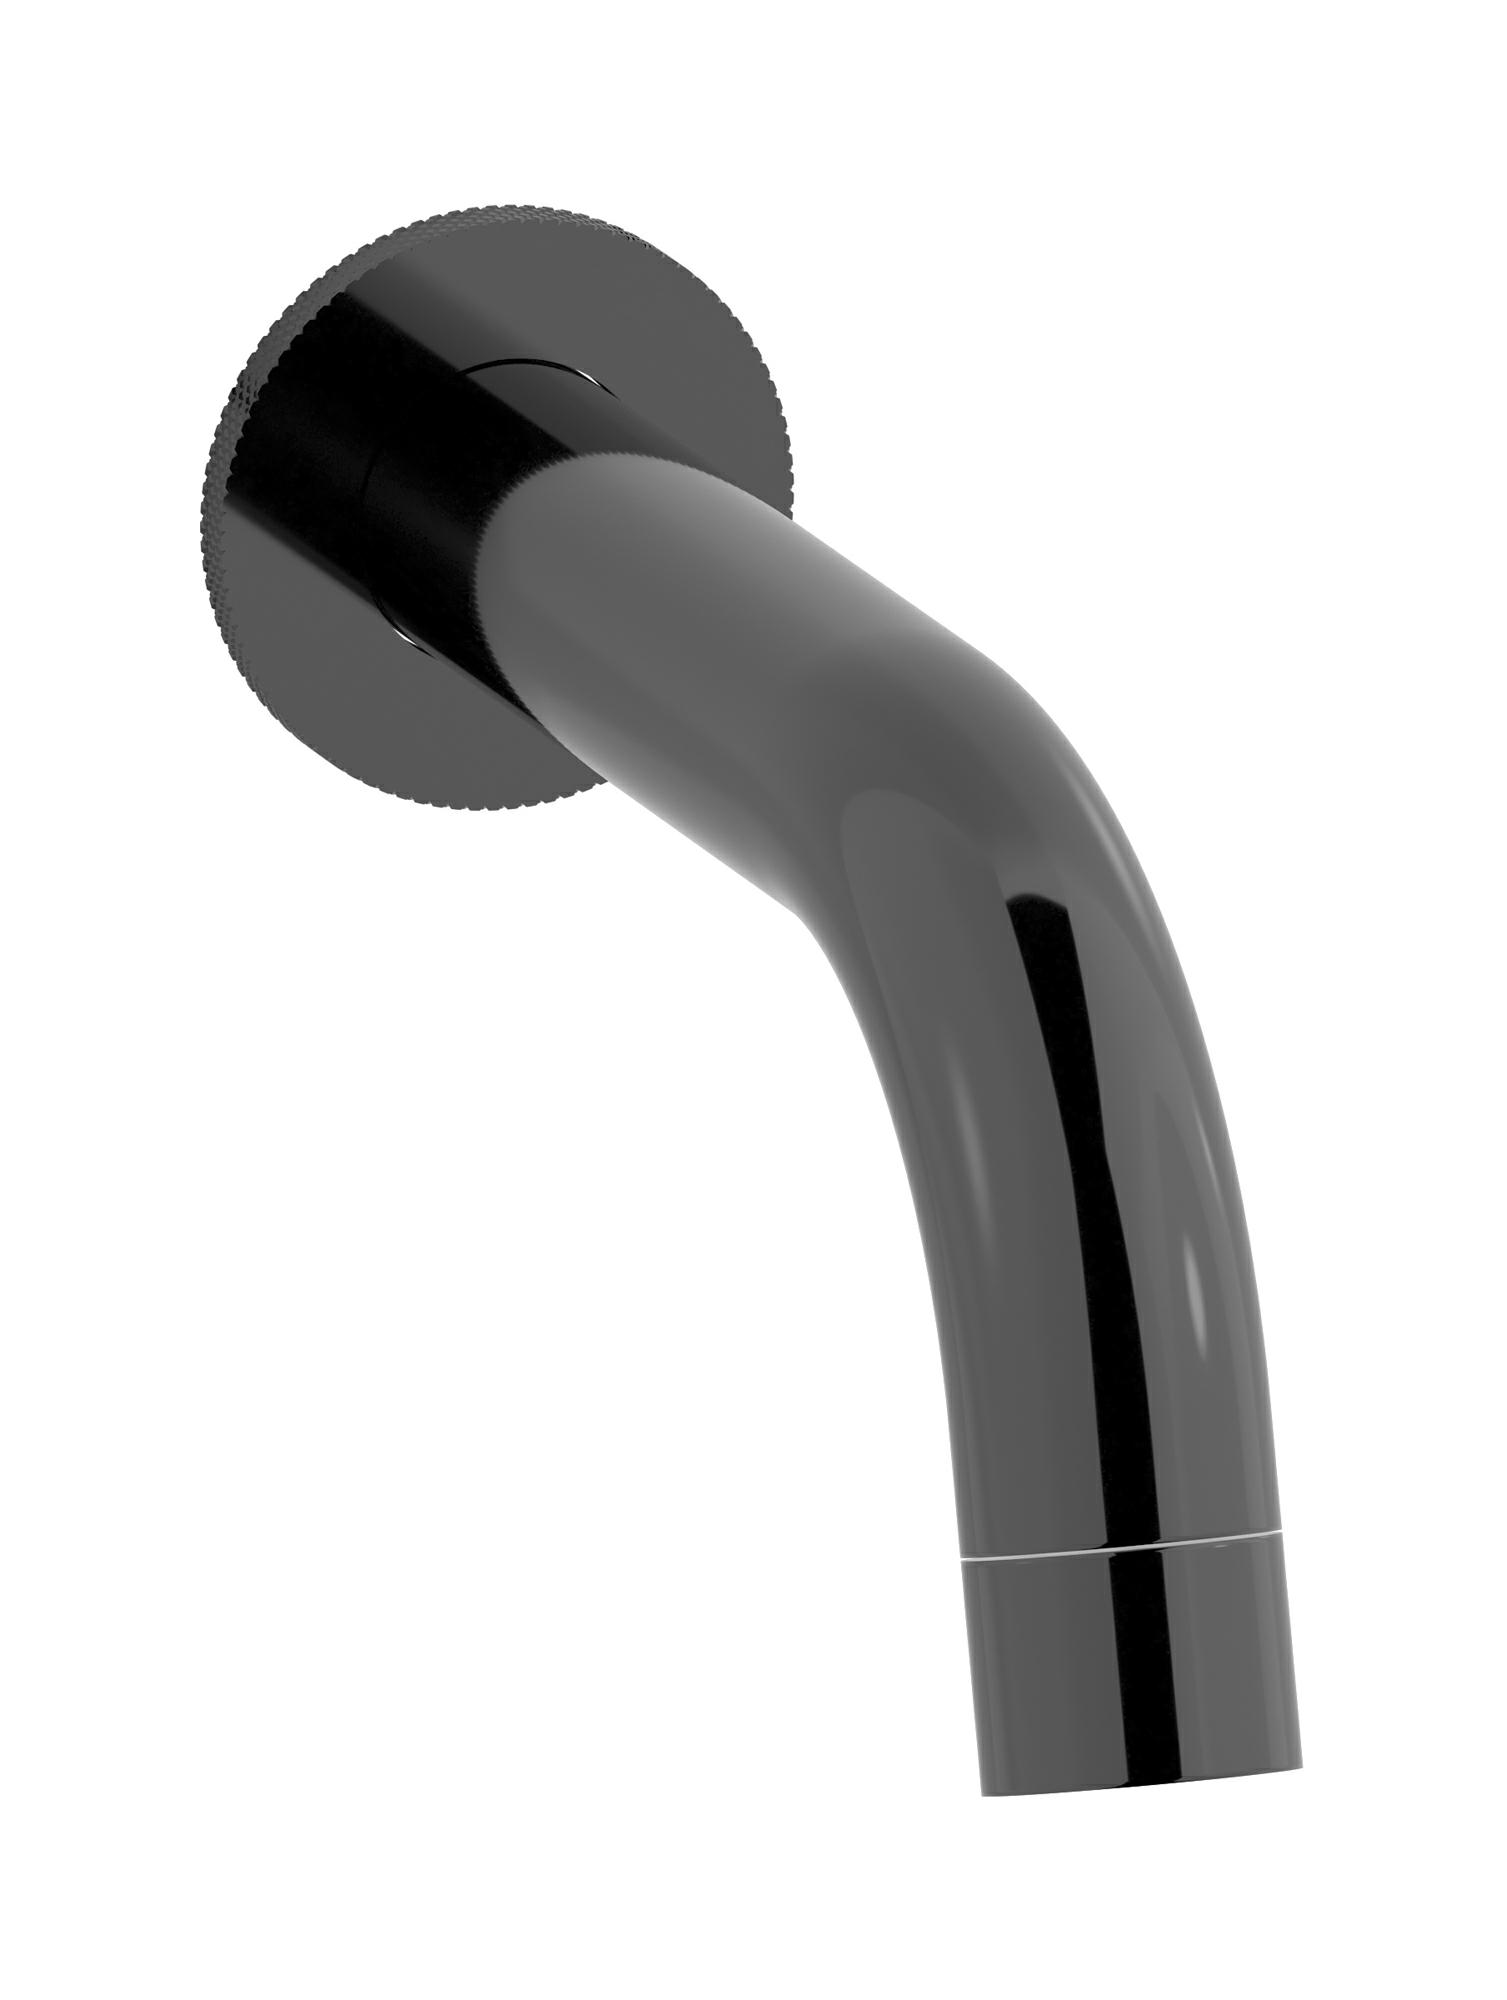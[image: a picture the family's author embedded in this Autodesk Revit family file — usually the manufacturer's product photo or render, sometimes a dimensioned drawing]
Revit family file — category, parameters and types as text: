
# Revit family: ID320
name_source: partatom
category: Apparecchi idraulici
units: mm (PartAtom-declared; Revit-internal decimal feet)

## family parameters
Basato su piano di lavoro = No
Condiviso = No
Mantieni orientamento annotazione = No
Numero OmniClass = 23.45.55.14
Punto di calcolo locali = No
Quota connettore circolare = Usa diametro
Sempre verticale = Sì
Taglio con vuoti quando caricato = No
Tipo di parte = Normale
Titolo OmniClass = Single Faucets

## types (11) — shared parameters
Commenti sul tipo = Spout
Connessione CW = No
Connessione HW = No
Connessione di scarico = No
Connessione di ventilazione = No
Descrizione = Wall mounted spout
Produttore = IB Rubinetterie S.p.A.
URL = https://www.weareib.it
Water inlet = 10 mm  [stored 0.0328084 ft]
zero-valued in all types: Prospetto di default

## per-type parameters (varying)
| type | Finishes surface | Immagine tipo | Modello |
| Chrome | IB_Chrome | ID320CC.jpg | ID320CC |
| Brushed nickel | IB_Brushed nickel | ID320SS.jpg | ID320SS |
| Natural brass | IB_Brass | ID320ON.jpg | ID320ON |
| Black chrome | IB_Black chrome | ID320CF.jpg | ID320CF |
| Brushed black chrome | IB_Brushed black chrome | ID320CS.jpg | ID320CS |
| Pale gold | IB_Pale gold | ID320II.jpg | ID320II |
| Brushed pale gold | IB_brushed pale gold | ID320IS.jpg | ID320IS |
| Rose gold | IB_Rose gold | ID320RS.jpg | ID320RS |
| Brushed rose gold | IB_Brushed rose gold | ID320SR.jpg | ID320SR |
| Gold | IB_gold | ID320OO.jpg | ID320OO |
| Brushed gold | IB_brushed gold | ID320OS.jpg | ID320OS |

note: [stored X ft] marks values corroborated as IEEE doubles in the binary element streams (Revit-internal decimal feet)
